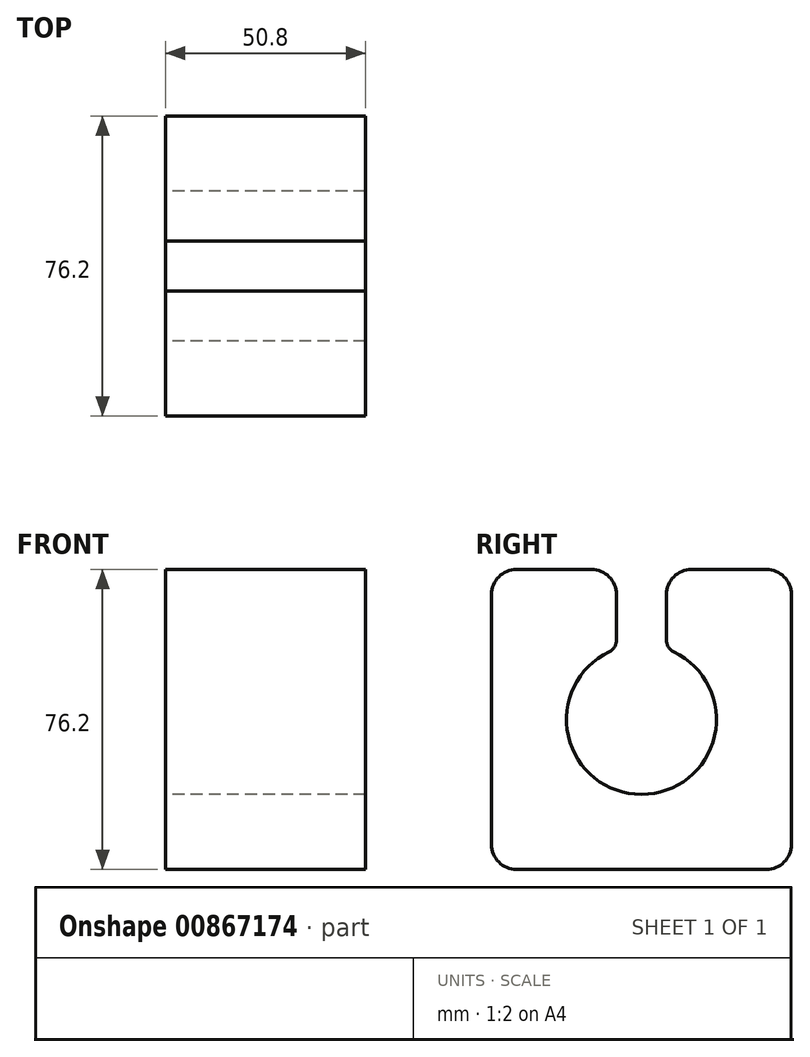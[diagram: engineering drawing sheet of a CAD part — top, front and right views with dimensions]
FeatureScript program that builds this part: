
annotation { "Feature Type Name" : "Feature", "Feature Type Description" : "" }
export const myFeature = defineFeature(function(context is Context, id is Id, definition is map)
    precondition{}
    {
        {
            var Q0;
            Q0=qCreatedBy(makeId("Right.planeOp"),FACE);
            var sketch = newSketch(context, id + "F0", { "sketchPlane" : qUnion([Q0])});
            skLineSegment(sketch, "E0.bottom", {"start": v(31.75, 38.1) * mm, "end": v(12.7, 38.1) * mm});
            skLineSegment(sketch, "E0.top", {"start": v(31.75, -38.1) * mm, "end": v(-31.75, -38.1) * mm});
            skLineSegment(sketch, "E0.left", {"start": v(38.1, 31.75) * mm, "end": v(38.1, -31.75) * mm});
            skLineSegment(sketch, "E0.right", {"start": v(-38.1, 31.75) * mm, "end": v(-38.1, -31.75) * mm});
            skPoint(sketch, "E0.middle", {"position": v(0, 0) * mm});
            skArc(sketch, "E1", {"start": v(-8.2, 17.2) * mm, "mid": v(0, -19.05) * mm, "end": v(8.2, 17.2) * mm});
            skLineSegment(sketch, "E2", {"start": v(6.35, 31.75) * mm, "end": v(6.35, 20.13) * mm});
            skLineSegment(sketch, "E3", {"start": v(-6.35, 20.13) * mm, "end": v(-6.35, 31.75) * mm});
            skLineSegment(sketch, "E4.trimOffspring", {"start": v(-12.7, 38.1) * mm, "end": v(-31.75, 38.1) * mm});
            skPoint(sketch, "E5.orphan", {"position": v(0, 38.1) * mm});
            skPoint(sketch, "E6.visualSharp", {"position": v(-38.1, -38.1) * mm});
            skArc(sketch, "E6.filletArc", {"start": v(-38.1, -31.75) * mm, "mid": v(-36.24, -36.24) * mm, "end": v(-31.75, -38.1) * mm});
            skPoint(sketch, "E7.visualSharp", {"position": v(38.1, -38.1) * mm});
            skArc(sketch, "E7.filletArc", {"start": v(31.75, -38.1) * mm, "mid": v(36.24, -36.24) * mm, "end": v(38.1, -31.75) * mm});
            skPoint(sketch, "E8.visualSharp", {"position": v(38.1, 38.1) * mm});
            skArc(sketch, "E8.filletArc", {"start": v(38.1, 31.75) * mm, "mid": v(36.24, 36.24) * mm, "end": v(31.75, 38.1) * mm});
            skPoint(sketch, "E9.visualSharp", {"position": v(-38.1, 38.1) * mm});
            skArc(sketch, "E9.filletArc", {"start": v(-31.75, 38.1) * mm, "mid": v(-36.24, 36.24) * mm, "end": v(-38.1, 31.75) * mm});
            skPoint(sketch, "E10.visualSharp", {"position": v(6.35, 38.1) * mm});
            skArc(sketch, "E10.filletArc", {"start": v(12.7, 38.1) * mm, "mid": v(8.2, 36.24) * mm, "end": v(6.35, 31.75) * mm});
            skPoint(sketch, "E11.visualSharp", {"position": v(-6.35, 38.1) * mm});
            skArc(sketch, "E11.filletArc", {"start": v(-6.35, 31.75) * mm, "mid": v(-8.2, 36.24) * mm, "end": v(-12.7, 38.1) * mm});
            skPoint(sketch, "E12.visualSharp", {"position": v(6.35, 17.96) * mm});
            skArc(sketch, "E12.filletArc", {"start": v(6.35, 20.13) * mm, "mid": v(6.85, 18.4) * mm, "end": v(8.2, 17.2) * mm});
            skPoint(sketch, "E13.visualSharp", {"position": v(-6.35, 17.96) * mm});
            skArc(sketch, "E13.filletArc", {"start": v(-8.2, 17.2) * mm, "mid": v(-6.85, 18.4) * mm, "end": v(-6.35, 20.13) * mm});
            skSolve(sketch);
        }
        {
            var Q0;
            Q0=makeQuery(id+"F0.imprint","IMPRINT",FACE,{"disambiguationData":[TD([[makeQuery(id+"F0.imprint","IMPRINT",EDGE,{"derivedFrom":sQuery(id+"F0.wireOp",EDGE,"E0.bottom")}),1.0]])]});
            extrude(context, id + "F1", {"entities" : qUnion([Q0]), "depth" : 50.8 * mm, "offsetDistance" : 25.4 * mm});
        }
    });
